# Revit family: Sirena_Aguilera Electronica
name_source: partatom
category: Dispositivos de alarma de incendios
revit_build: Autodesk Revit 2017 (Build: 20160225_1515(x64)
units: mm (PartAtom-declared; Revit-internal decimal feet)

## family parameters
Anfitrión = Cara
Compartido = No
Corte con vacíos al cargar = No
Cota de conector redondo = Diámetro de uso
Mantener orientación de anotación = Sí
Número OmniClass = 23.85.30.21.14.11
Punto de cálculo de habitación = No
Tipo de pieza = Normal
Título OmniClass = Concentration Detection Bells and Sounders

## types (2) — shared parameters
Altura 1 = 10 mm  [stored 0.0328084 ft]
Altura 2 = 53 mm  [stored 0.173885 ft]
Altura 3 = 17 mm
Diámetro tubo = 20 mm  [stored 0.0656168 ft]
Elevación por defecto = 1200 mm
Fabricante = Aguilera Electrónica
Símbolo = Sí
Símbolo texto modelo = Sí
URL = https://aguilera.es

## per-type parameters (varying)
| type | Descripción | Flash | Modelo |
| Sirena electrónica | Sirena de bajo consumo multitono. Certificada según EN 54-3. Consumo entre 6 y 33 mA, dependiendo del tono. Dimensiones: Ø 93 mm, altura: 63mm.

Nivel sonoro: 102 dB (tono 3). Protección: IP54 (con base baja) IP65 (con base alta) | No | AE/V-AS1SB |
| Sirena electrónica con foco | Sirena con foco multitono. Certificada según EN 54-3. Dimensiones: Ø 93 mm, altura: 80 mm. Nivel sonoro: 100 dB (tono 3). Intensidad luminosa: > 0,5Cd.

Consumo: 25mA. Protección: IP54 (con base baja) IP65 (con base alta) | Sí | AE/V-ASF1SB |

note: [stored X ft] marks values corroborated as IEEE doubles in the binary element streams (Revit-internal decimal feet)
